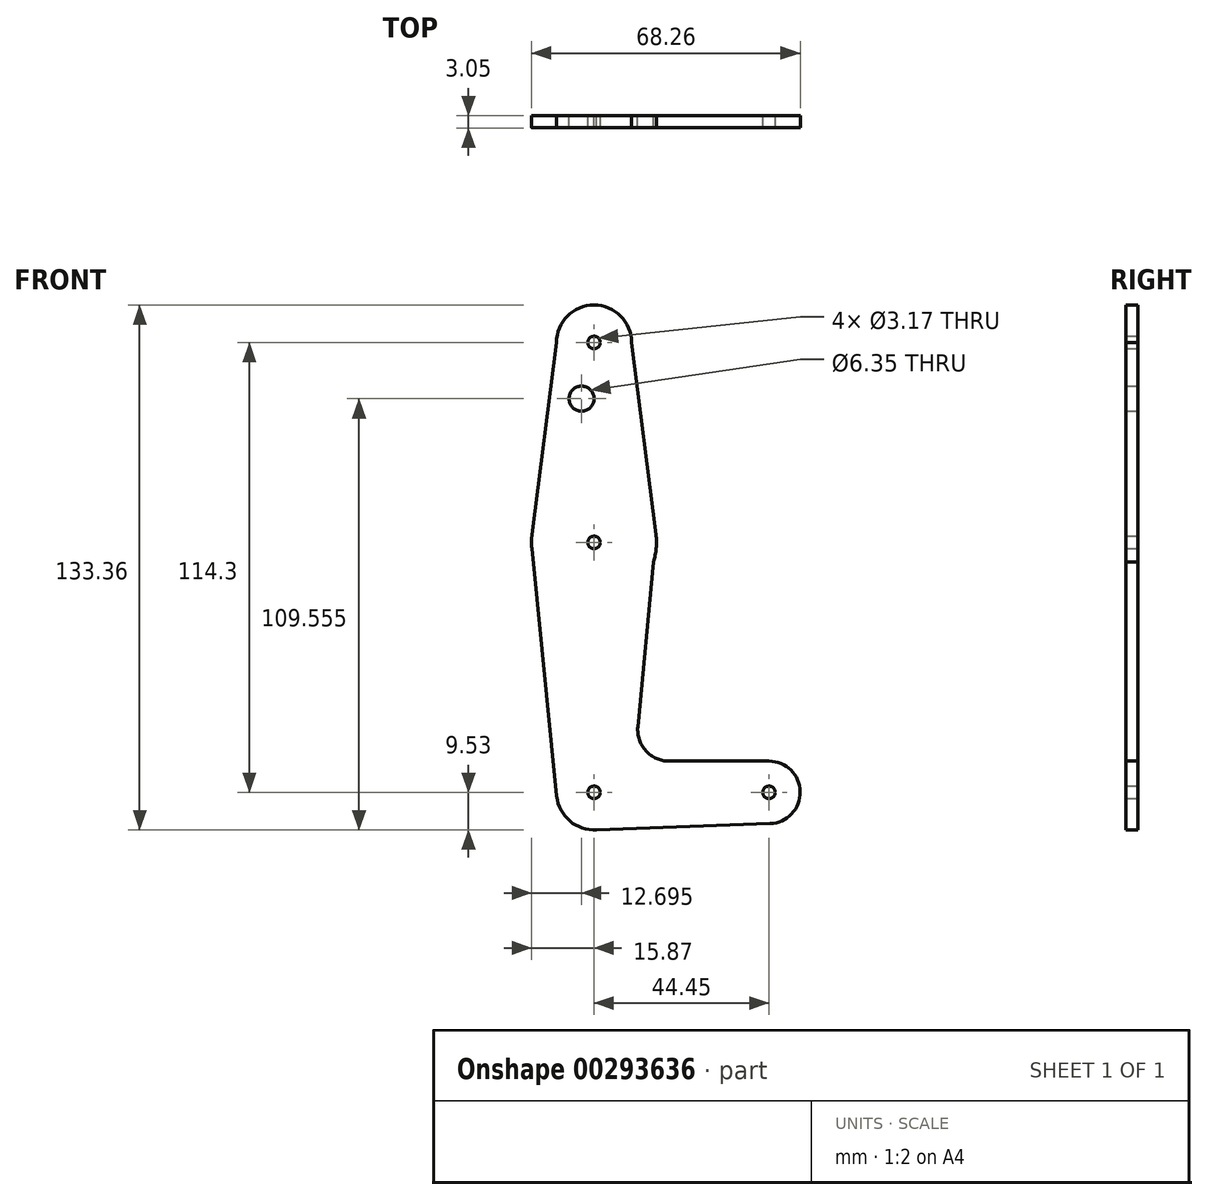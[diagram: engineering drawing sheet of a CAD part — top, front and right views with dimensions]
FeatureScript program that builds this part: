
annotation { "Feature Type Name" : "Feature", "Feature Type Description" : "" }
export const myFeature = defineFeature(function(context is Context, id is Id, definition is map)
    precondition{}
    {
        {
            var Q0;
            Q0=qCreatedBy(makeId("Front.planeOp"),FACE);
            var sketch = newSketch(context, id + "F0", { "sketchPlane" : qUnion([Q0])});
            skLineSegment(sketch, "E0", {"start": v(0, 0) * mm, "end": v(0, 63.5) * mm});
            skLineSegment(sketch, "E1", {"start": v(0, 63.5) * mm, "end": v(0, 114.3) * mm});
            skLineSegment(sketch, "E2", {"start": v(0, 0) * mm, "end": v(44.45, 0) * mm});
            skCircle(sketch, "E3", {"center": v(44.45, 0) * mm, "radius": 7.94 * mm});
            skCircle(sketch, "E4", {"center": v(0, 114.3) * mm, "radius": 9.53 * mm});
            skCircle(sketch, "E5", {"center": v(0, 63.5) * mm, "radius": 15.88 * mm});
            skCircle(sketch, "E6", {"center": v(0, 0) * mm, "radius": 9.53 * mm});
            skLineSegment(sketch, "E7", {"start": v(-15.75, 65.5) * mm, "end": v(-9.52, 114.3) * mm});
            skLineSegment(sketch, "E8", {"start": v(9.53, 114.3) * mm, "end": v(15.75, 65.5) * mm});
            skLineSegment(sketch, "E9", {"start": v(15.75, 65.5) * mm, "end": v(11.14, 16.63) * mm});
            skLineSegment(sketch, "E10", {"start": v(19.05, 7.94) * mm, "end": v(44.45, 7.94) * mm});
            skCircle(sketch, "E11", {"center": v(0, 114.3) * mm, "radius": 1.59 * mm});
            skCircle(sketch, "E12", {"center": v(0, 63.5) * mm, "radius": 1.59 * mm});
            skCircle(sketch, "E13", {"center": v(0, 0) * mm, "radius": 1.59 * mm});
            skCircle(sketch, "E14", {"center": v(44.45, 0) * mm, "radius": 1.59 * mm});
            skCircle(sketch, "E15", {"center": v(-3.18, 100.03) * mm, "radius": 3.18 * mm});
            skLineSegment(sketch, "E16", {"start": v(-15.8, 61.91) * mm, "end": v(-9.48, -0.95) * mm});
            skLineSegment(sketch, "E17", {"start": v(0, -9.53) * mm, "end": v(44.73, -7.93) * mm});
            skArc(sketch, "E18.filletArc", {"start": v(11.14, 16.63) * mm, "mid": v(13.17, 10.54) * mm, "end": v(19.05, 7.94) * mm});
            skSolve(sketch);
        }
        {
            var Q0;
            Q0 = qSketchRegion(id + "F0", true);
            var Q1;
            {var subQ0=sQuery(id+"F0.wireOp",EDGE,"E13");var subQ1=sQuery(id+"F0.wireOp",EDGE,"E0");var subQ2=makeQuery(id+"F0.imprint","INTERSECT",VERTEX,{"derivedFrom":[subQ1,subQ0]});Q1=makeQuery(id+"F0.imprint","IMPRINT",FACE,{"disambiguationData":[TD([[makeQuery(id+"F0.imprint","IMPRINT",EDGE,{"disambiguationData":[TD([[subQ2,-1.0]])],"derivedFrom":subQ1}),-1.0]])]});}
            extrude(context, id + "F1", {"entities" : qUnion([Q0, Q1]), "depth" : 3.05 * mm});
        }
    });
